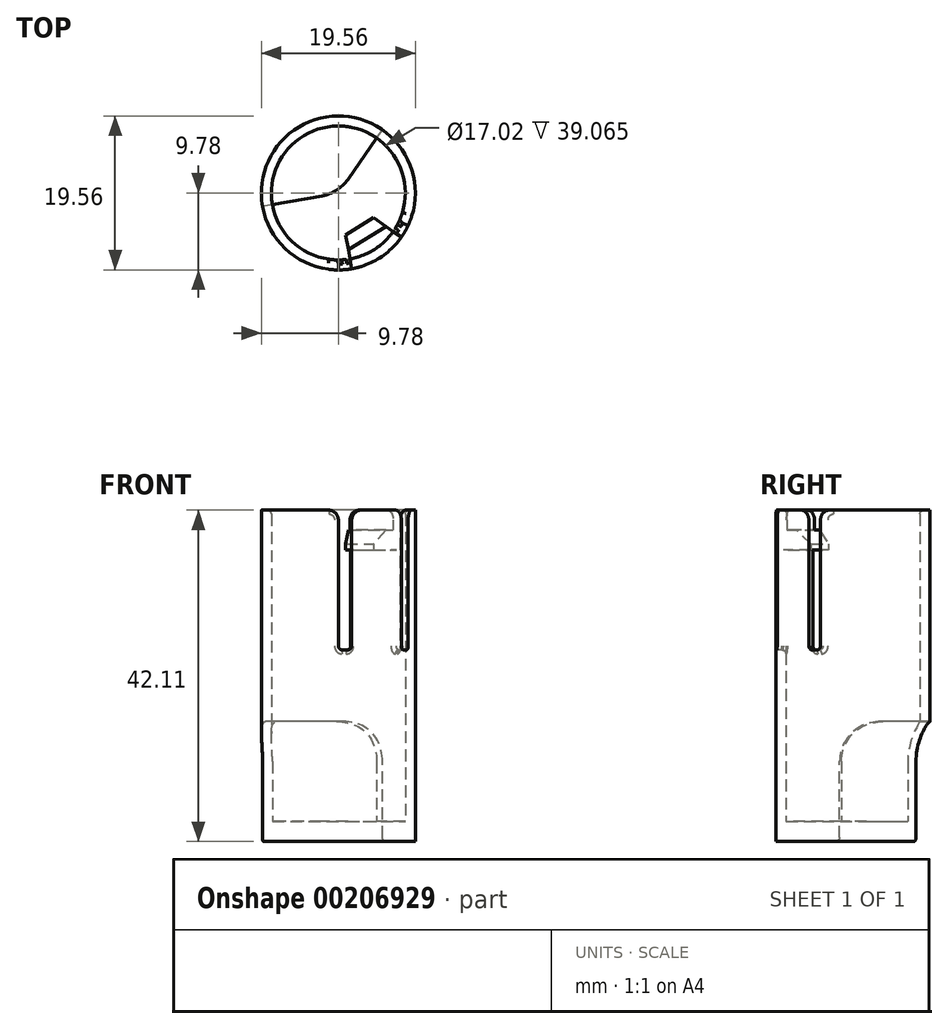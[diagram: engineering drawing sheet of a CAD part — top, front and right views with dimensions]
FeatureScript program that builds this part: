
annotation { "Feature Type Name" : "Feature", "Feature Type Description" : "" }
export const myFeature = defineFeature(function(context is Context, id is Id, definition is map)
    precondition{}
    {
        {
            var Q0;
            Q0=qCreatedBy(makeId("Top.planeOp"),FACE);
            var sketch = newSketch(context, id + "F0", { "sketchPlane" : qUnion([Q0])});
            skCircle(sketch, "E0", {"center": v(0, 0) * mm, "radius": 8.5 * mm});
            skCircle(sketch, "E1", {"center": v(0, 0) * mm, "radius": 9.78 * mm});
            skSolve(sketch);
        }
        {
            var Q0;
            Q0 = qSketchRegion(id + "F0", true);
            extrude(context, id + "F1", {"entities" : qUnion([Q0]), "depth" : 34.5 * mm});
        }
        {
            var Q0;
            Q0=makeQuery(id+"F1.opExtrude","CAP_FACE",FACE,{"disambiguationData":[OSD([sQuery(id+"F0.wireOp",EDGE,"E0"),sQuery(id+"F0.wireOp",EDGE,"E1")])],"isStart":false});
            var sketch = newSketch(context, id + "F2", { "sketchPlane" : qUnion([Q0])});
            skCircle(sketch, "E2.0", {"center": v(0, 0) * mm, "radius": 8.5 * mm, "construction": true});
            skLineSegment(sketch, "E3", {"start": v(0, 0) * mm, "end": v(6.97, -4.88) * mm, "construction": true});
            skLineSegment(sketch, "E4", {"start": v(0, 0) * mm, "end": v(1.48, -8.38) * mm, "construction": true});
            skLineSegment(sketch, "E5", {"start": v(0, 0) * mm, "end": v(0, -8.5) * mm, "construction": true});
            skLineSegment(sketch, "E6", {"start": v(0, 0) * mm, "end": v(7.71, -3.6) * mm, "construction": true});
            skSolve(sketch);
        }
        {
            var Q0;
            Q0=makeQuery(id+"F2.imprint","IMPRINT",FACE,{"disambiguationData":[TD([[makeQuery(id+"F2.imprint","IMPRINT",EDGE,{"derivedFrom":makeQuery(id+"F1.opExtrude","CAP_EDGE",EDGE,{"disambiguationData":[OSD([sQuery(id+"F0.wireOp",EDGE,"E0")])],"isStart":false})}),-1.0]])]});
            var sketch = newSketch(context, id + "F3", { "sketchPlane" : qUnion([Q0])});
            skLineSegment(sketch, "E7.0", {"start": v(0.94, -5.33) * mm, "end": v(1.48, -8.38) * mm});
            skLineSegment(sketch, "E7.1", {"start": v(4.47, -3.13) * mm, "end": v(6.97, -4.88) * mm});
            skArc(sketch, "E7.2", {"start": v(1.7, -9.63) * mm, "mid": v(5.25, -8.25) * mm, "end": v(8.01, -5.6) * mm});
            skLineSegment(sketch, "E8", {"start": v(1.48, -8.38) * mm, "end": v(1.7, -9.63) * mm});
            skLineSegment(sketch, "E9", {"start": v(6.97, -4.88) * mm, "end": v(8.01, -5.6) * mm});
            skLineSegment(sketch, "E10", {"start": v(0.94, -5.33) * mm, "end": v(4.47, -3.13) * mm});
            skSolve(sketch);
        }
        {
            var Q0;
            Q0 = qSketchRegion(id + "F3", true);
            extrude(context, id + "F4", {"entities" : qUnion([Q0]), "operationType" : NewBodyOperationType.ADD, "depth" : 2.54 * mm});
        }
        {
            var Q0;
            Q0=makeQuery(id+"F2.imprint","IMPRINT",FACE,{"disambiguationData":[TD([[makeQuery(id+"F2.imprint","IMPRINT",EDGE,{"derivedFrom":makeQuery(id+"F1.opExtrude","CAP_EDGE",EDGE,{"disambiguationData":[OSD([sQuery(id+"F0.wireOp",EDGE,"E0")])],"isStart":false})}),-1.0]])]});
            var sketch = newSketch(context, id + "F5", { "sketchPlane" : qUnion([Q0])});
            skLineSegment(sketch, "E11.0", {"start": v(0, 0) * mm, "end": v(0, -8.5) * mm, "construction": true});
            skLineSegment(sketch, "E11.1", {"start": v(0, 0) * mm, "end": v(7.71, -3.6) * mm, "construction": true});
            skArc(sketch, "E12.0", {"start": v(8.86, -4.13) * mm, "mid": v(-5.25, 8.25) * mm, "end": v(0, -9.78) * mm});
            skLineSegment(sketch, "E13", {"start": v(0, -8.5) * mm, "end": v(0, -9.78) * mm});
            skLineSegment(sketch, "E14", {"start": v(7.71, -3.6) * mm, "end": v(8.86, -4.13) * mm});
            skArc(sketch, "E15.0", {"start": v(7.71, -3.6) * mm, "mid": v(-4.57, 7.18) * mm, "end": v(0, -8.5) * mm});
            skPoint(sketch, "E16.orphan", {"position": v(1.7, -9.63) * mm});
            skPoint(sketch, "E17.orphan", {"position": v(8.01, -5.6) * mm});
            skSolve(sketch);
        }
        {
            var Q0;
            Q0 = qSketchRegion(id + "F5", true);
            extrude(context, id + "F6", {"entities" : qUnion([Q0]), "operationType" : NewBodyOperationType.ADD, "depth" : 5.08 * mm});
        }
        {
            var Q0;
            Q0=makeQuery(id+"F2.imprint","IMPRINT",FACE,{"disambiguationData":[TD([[makeQuery(id+"F2.imprint","IMPRINT",EDGE,{"derivedFrom":makeQuery(id+"F1.opExtrude","CAP_EDGE",EDGE,{"disambiguationData":[OSD([sQuery(id+"F0.wireOp",EDGE,"E0")])],"isStart":false})}),-1.0]])]});
            var sketch = newSketch(context, id + "F7", { "sketchPlane" : qUnion([Q0])});
            skLineSegment(sketch, "E18.0", {"start": v(1.48, -8.38) * mm, "end": v(1.7, -9.63) * mm});
            skArc(sketch, "E18.1", {"start": v(0, -9.78) * mm, "mid": v(0.85, -9.74) * mm, "end": v(1.7, -9.63) * mm});
            skArc(sketch, "E18.2", {"start": v(0, -8.5) * mm, "mid": v(0.74, -8.48) * mm, "end": v(1.48, -8.38) * mm});
            skLineSegment(sketch, "E18.3", {"start": v(0, -8.5) * mm, "end": v(0, -9.78) * mm});
            skLineSegment(sketch, "E18.4", {"start": v(7.71, -3.6) * mm, "end": v(8.86, -4.13) * mm});
            skArc(sketch, "E18.5", {"start": v(8.01, -5.6) * mm, "mid": v(8.47, -4.89) * mm, "end": v(8.86, -4.13) * mm});
            skLineSegment(sketch, "E18.6", {"start": v(6.97, -4.88) * mm, "end": v(8.01, -5.6) * mm});
            skArc(sketch, "E19.trimOffspring", {"start": v(6.97, -4.88) * mm, "mid": v(7.37, -4.25) * mm, "end": v(7.71, -3.6) * mm});
            skSolve(sketch);
        }
        {
            var Q0;
            Q0 = qSketchRegion(id + "F7", true);
            extrude(context, id + "F8", {"entities" : qUnion([Q0]), "operationType" : NewBodyOperationType.REMOVE, "oppositeDirection" : true, "depth" : 12.7 * mm});
        }
        {
            var Q0;
            Q0=makeQuery(id+"F1.opExtrude","CAP_FACE",FACE,{"disambiguationData":[OSD([sQuery(id+"F0.wireOp",EDGE,"E0"),sQuery(id+"F0.wireOp",EDGE,"E1")])],"isStart":true});
            var sketch = newSketch(context, id + "F9", { "sketchPlane" : qUnion([Q0])});
            skLineSegment(sketch, "E20.0", {"start": v(0, 0) * mm, "end": v(7.71, 3.6) * mm, "construction": true});
            skLineSegment(sketch, "E20.1", {"start": v(0, 0) * mm, "end": v(0, 8.5) * mm, "construction": true});
            skLineSegment(sketch, "E21", {"start": v(0, 0) * mm, "end": v(4.88, -6.97) * mm});
            skLineSegment(sketch, "E22", {"start": v(0, 0) * mm, "end": v(-8.38, 1.48) * mm});
            skSolve(sketch);
        }
        {
            var Q0;
            Q0=makeQuery(id+"F9.imprint","IMPRINT",FACE,{"disambiguationData":[TD([[makeQuery(id+"F9.imprint","IMPRINT",EDGE,{"derivedFrom":makeQuery(id+"F1.opExtrude","CAP_EDGE",EDGE,{"disambiguationData":[OSD([sQuery(id+"F0.wireOp",EDGE,"E1")])],"isStart":true})}),-1.0]])]});
            var sketch = newSketch(context, id + "F10", { "sketchPlane" : qUnion([Q0])});
            skArc(sketch, "E23.0", {"start": v(5.6, -8.01) * mm, "mid": v(5.25, 8.25) * mm, "end": v(-9.63, 1.7) * mm});
            skLineSegment(sketch, "E24.0", {"start": v(0, 0) * mm, "end": v(4.88, -6.97) * mm});
            skLineSegment(sketch, "E25.0", {"start": v(0, 0) * mm, "end": v(-8.38, 1.48) * mm});
            skLineSegment(sketch, "E26", {"start": v(4.88, -6.97) * mm, "end": v(5.6, -8.01) * mm});
            skLineSegment(sketch, "E27", {"start": v(-8.38, 1.48) * mm, "end": v(-9.63, 1.7) * mm});
            skSolve(sketch);
        }
        {
            var Q0;
            Q0 = qSketchRegion(id + "F10", true);
            extrude(context, id + "F11", {"entities" : qUnion([Q0]), "operationType" : NewBodyOperationType.ADD, "depth" : 2.54 * mm});
        }
        {
            var Q0;
            Q0=makeQuery(id+"F9.imprint","IMPRINT",FACE,{"disambiguationData":[TD([[makeQuery(id+"F9.imprint","IMPRINT",EDGE,{"derivedFrom":makeQuery(id+"F1.opExtrude","CAP_EDGE",EDGE,{"disambiguationData":[OSD([sQuery(id+"F0.wireOp",EDGE,"E1")])],"isStart":true})}),-1.0]])]});
            var sketch = newSketch(context, id + "F12", { "sketchPlane" : qUnion([Q0])});
            skLineSegment(sketch, "E28.0", {"start": v(4.88, -6.97) * mm, "end": v(5.6, -8.01) * mm});
            skArc(sketch, "E28.1", {"start": v(5.6, -8.01) * mm, "mid": v(-5.25, -8.25) * mm, "end": v(-9.63, 1.7) * mm});
            skArc(sketch, "E28.2", {"start": v(4.88, -6.97) * mm, "mid": v(-4.57, -7.18) * mm, "end": v(-8.38, 1.48) * mm});
            skLineSegment(sketch, "E28.3", {"start": v(-8.38, 1.48) * mm, "end": v(-9.63, 1.7) * mm});
            skSolve(sketch);
        }
        {
            var Q0;
            Q0 = qSketchRegion(id + "F12", true);
            extrude(context, id + "F13", {"entities" : qUnion([Q0]), "operationType" : NewBodyOperationType.REMOVE, "oppositeDirection" : true, "depth" : 12.7 * mm});
        }
        {
            var Q0;
            Q0=makeQuery(id+"F11.opExtrude","SWEPT_EDGE",EDGE,{"disambiguationData":[OSD([sQuery(id+"F10.wireOp",EDGE,"E24.0"),sQuery(id+"F10.wireOp",EDGE,"E25.0")])]});
            var Q1;
            Q1=makeQuery(id+"F13.boolean.opBoolean","COPY",EDGE,{"derivedFrom":makeQuery(id+"F13.opExtrude","CAP_EDGE",EDGE,{"disambiguationData":[OSD([sQuery(id+"F12.wireOp",EDGE,"E28.0")])],"isStart":false})});
            var Q2;
            Q2=makeQuery(id+"F13.boolean.opBoolean","COPY",EDGE,{"derivedFrom":makeQuery(id+"F13.opExtrude","CAP_EDGE",EDGE,{"disambiguationData":[OSD([sQuery(id+"F12.wireOp",EDGE,"E28.3")])],"isStart":false})});
            fillet(context, id + "F14", {"entities" : qUnion([Q0, Q1, Q2]), "radius" : 5.08 * mm, "tangentPropagation" : true, "allowEdgeOverflow" : false});
        }
        {
            var Q0;
            Q0=makeQuery(id+"F8.boolean.opBoolean","COPY",EDGE,{"derivedFrom":makeQuery(id+"F8.opExtrude","CAP_EDGE",EDGE,{"disambiguationData":[OSD([sQuery(id+"F7.wireOp",EDGE,"E18.4")])],"isStart":false})});
            var Q1;
            Q1=makeQuery(id+"F8.boolean.opBoolean","COPY",EDGE,{"derivedFrom":makeQuery(id+"F8.opExtrude","CAP_EDGE",EDGE,{"disambiguationData":[OSD([sQuery(id+"F7.wireOp",EDGE,"E18.6")])],"isStart":false})});
            var Q2;
            Q2=makeQuery(id+"F8.boolean.opBoolean","COPY",EDGE,{"derivedFrom":makeQuery(id+"F8.opExtrude","CAP_EDGE",EDGE,{"disambiguationData":[OSD([sQuery(id+"F7.wireOp",EDGE,"E18.0")])],"isStart":false})});
            var Q3;
            Q3=makeQuery(id+"F8.boolean.opBoolean","COPY",EDGE,{"derivedFrom":makeQuery(id+"F8.opExtrude","CAP_EDGE",EDGE,{"disambiguationData":[OSD([sQuery(id+"F7.wireOp",EDGE,"E18.3")])],"isStart":false})});
            fillet(context, id + "F15", {"entities" : qUnion([Q0, Q1, Q2, Q3]), "radius" : 0.5 * mm, "tangentPropagation" : true, "allowEdgeOverflow" : false});
        }
        {
            var Q0;
            Q0=makeQuery(id+"F4.opExtrude","CAP_EDGE",EDGE,{"disambiguationData":[OSD([sQuery(id+"F3.wireOp",EDGE,"E10")])],"isStart":false});
            chamfer(context, id + "F16", {"entities" : qUnion([Q0]), "width" : 1.78 * mm, "tangentPropagation" : true});
        }
        {
            var Q0;
            Q0=makeQuery(id+"F4.opExtrude","CAP_FACE",FACE,{"disambiguationData":[OSD([sQuery(id+"F3.wireOp",EDGE,"E7.0"),sQuery(id+"F3.wireOp",EDGE,"E7.1"),sQuery(id+"F3.wireOp",EDGE,"E7.2"),sQuery(id+"F3.wireOp",EDGE,"E8"),sQuery(id+"F3.wireOp",EDGE,"E9"),sQuery(id+"F3.wireOp",EDGE,"E10")])],"isStart":false});
            var sketch = newSketch(context, id + "F17", { "sketchPlane" : qUnion([Q0])});
            skArc(sketch, "E29.0", {"start": v(1.48, -8.38) * mm, "mid": v(4.57, -7.18) * mm, "end": v(6.97, -4.88) * mm});
            skLineSegment(sketch, "E30.0", {"start": v(1.48, -8.38) * mm, "end": v(1.7, -9.63) * mm});
            skLineSegment(sketch, "E30.1", {"start": v(6.97, -4.88) * mm, "end": v(8.01, -5.6) * mm});
            skArc(sketch, "E30.2", {"start": v(1.7, -9.63) * mm, "mid": v(5.25, -8.25) * mm, "end": v(8.01, -5.6) * mm});
            skPoint(sketch, "E31.orphan", {"position": v(1.27, -7.22) * mm});
            skPoint(sketch, "E32.orphan", {"position": v(6.06, -4.24) * mm});
            skSolve(sketch);
        }
        {
            var Q0;
            Q0 = qSketchRegion(id + "F17", true);
            extrude(context, id + "F18", {"entities" : qUnion([Q0]), "operationType" : NewBodyOperationType.ADD, "depth" : 2.54 * mm});
        }
        {
            var Q0;
            Q0=makeQuery(id+"F6.opExtrude","CAP_EDGE",EDGE,{"disambiguationData":[OSD([sQuery(id+"F5.wireOp",EDGE,"E13")])],"isStart":false});
            var Q1;
            Q1=makeQuery(id+"F18.opExtrude","CAP_EDGE",EDGE,{"disambiguationData":[OSD([sQuery(id+"F17.wireOp",EDGE,"E30.0")])],"isStart":false});
            var Q2;
            Q2=makeQuery(id+"F18.opExtrude","CAP_EDGE",EDGE,{"disambiguationData":[OSD([sQuery(id+"F17.wireOp",EDGE,"E30.1")])],"isStart":false});
            var Q3;
            Q3=makeQuery(id+"F6.opExtrude","CAP_EDGE",EDGE,{"disambiguationData":[OSD([sQuery(id+"F5.wireOp",EDGE,"E14")])],"isStart":false});
            fillet(context, id + "F19", {"entities" : qUnion([Q0, Q1, Q2, Q3]), "radius" : 1.27 * mm, "tangentPropagation" : true, "allowEdgeOverflow" : false});
        }
        {
            var Q0;
            Q0=makeQuery(id+"F6.opExtrude","CAP_EDGE",EDGE,{"disambiguationData":[OSD([sQuery(id+"F5.wireOp",EDGE,"E15.0")])],"isStart":false});
            fillet(context, id + "F20", {"entities" : qUnion([Q0]), "radius" : 0.5 * mm, "tangentPropagation" : true, "allowEdgeOverflow" : false});
        }
        {
            var Q0;
            Q0=makeQuery(id+"F11.opExtrude","CAP_EDGE",EDGE,{"disambiguationData":[OSD([sQuery(id+"F10.wireOp",EDGE,"E24.0"),sQuery(id+"F10.wireOp",EDGE,"E26")])],"isStart":false});
            fillet(context, id + "F21", {"entities" : qUnion([Q0]), "radius" : 0.5 * mm, "tangentPropagation" : true, "allowEdgeOverflow" : false});
        }
    });
